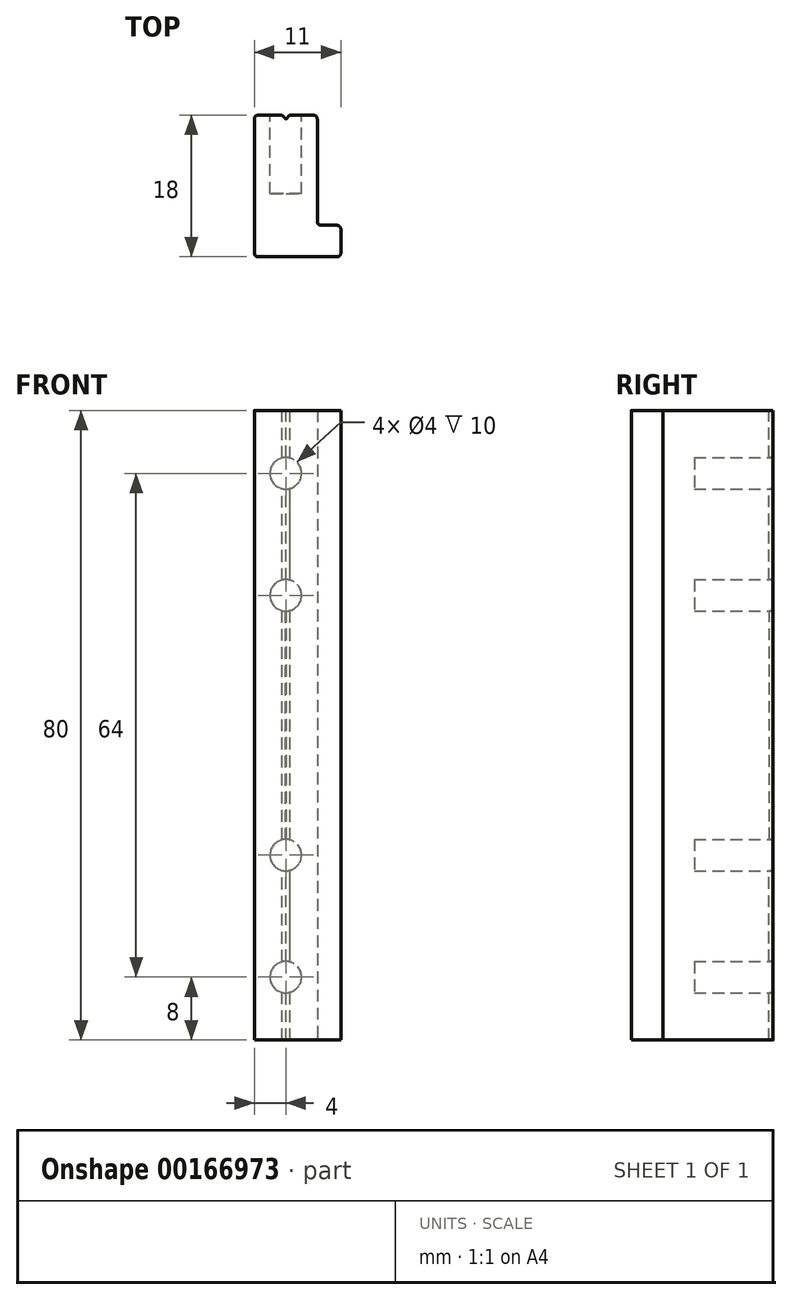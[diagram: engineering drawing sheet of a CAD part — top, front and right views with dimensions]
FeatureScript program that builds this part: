
annotation { "Feature Type Name" : "Feature", "Feature Type Description" : "" }
export const myFeature = defineFeature(function(context is Context, id is Id, definition is map)
    precondition{}
    {
        {
            var Q0;
            Q0=qCreatedBy(makeId("Top.planeOp"),FACE);
            var sketch = newSketch(context, id + "F0", { "sketchPlane" : qUnion([Q0])});
            skLineSegment(sketch, "E0", {"start": v(0, 0) * mm, "end": v(0, 18) * mm});
            skLineSegment(sketch, "E1", {"start": v(0, 18) * mm, "end": v(8, 18) * mm});
            skLineSegment(sketch, "E2", {"start": v(8, 18) * mm, "end": v(8, 4) * mm});
            skLineSegment(sketch, "E3", {"start": v(8, 4) * mm, "end": v(11, 4) * mm});
            skLineSegment(sketch, "E4", {"start": v(11, 4) * mm, "end": v(11, 0) * mm});
            skLineSegment(sketch, "E5", {"start": v(11, 0) * mm, "end": v(0, 0) * mm});
            skSolve(sketch);
        }
        {
            var Q0;
            Q0=makeQuery(id+"F0.imprint","IMPRINT",FACE,{"disambiguationData":[TD([[makeQuery(id+"F0.imprint","IMPRINT",EDGE,{"derivedFrom":sQuery(id+"F0.wireOp",EDGE,"E0")}),-1.0]])]});
            extrude(context, id + "F1", {"entities" : qUnion([Q0]), "depth" : 80 * mm});
        }
        {
            var Q0;
            Q0=makeQuery(id+"F1.opExtrude","SWEPT_FACE",FACE,{"disambiguationData":[OSD([sQuery(id+"F0.wireOp",EDGE,"E1")])]});
            var sketch = newSketch(context, id + "F2", { "sketchPlane" : qUnion([Q0])});
            skCircle(sketch, "E6", {"center": v(-4, 72) * mm, "radius": 2 * mm});
            skCircle(sketch, "E7", {"center": v(-4, 56.5) * mm, "radius": 2 * mm});
            skCircle(sketch, "E8", {"center": v(-4, 23.5) * mm, "radius": 2 * mm});
            skCircle(sketch, "E9", {"center": v(-4, 8) * mm, "radius": 2 * mm});
            skLineSegment(sketch, "E10", {"start": v(-4, 80) * mm, "end": v(-4, 0) * mm, "construction": true});
            skSolve(sketch);
        }
        {
            var Q0;
            Q0=makeQuery(id+"F2.imprint","IMPRINT",FACE,{"disambiguationData":[TD([[makeQuery(id+"F2.imprint","IMPRINT",EDGE,{"derivedFrom":sQuery(id+"F2.wireOp",EDGE,"E6")}),1.0]])]});
            var Q1;
            Q1=makeQuery(id+"F2.imprint","IMPRINT",FACE,{"disambiguationData":[TD([[makeQuery(id+"F2.imprint","IMPRINT",EDGE,{"derivedFrom":sQuery(id+"F2.wireOp",EDGE,"E7")}),1.0]])]});
            var Q2;
            Q2=makeQuery(id+"F2.imprint","IMPRINT",FACE,{"disambiguationData":[TD([[makeQuery(id+"F2.imprint","IMPRINT",EDGE,{"derivedFrom":sQuery(id+"F2.wireOp",EDGE,"E8")}),1.0]])]});
            var Q3;
            Q3=makeQuery(id+"F2.imprint","IMPRINT",FACE,{"disambiguationData":[TD([[makeQuery(id+"F2.imprint","IMPRINT",EDGE,{"derivedFrom":sQuery(id+"F2.wireOp",EDGE,"E9")}),1.0]])]});
            extrude(context, id + "F3", {"entities" : qUnion([Q0, Q1, Q2, Q3]), "operationType" : NewBodyOperationType.REMOVE, "oppositeDirection" : true, "depth" : 10 * mm});
        }
        {
            var Q0;
            Q0=makeQuery(id+"F1.opExtrude","CAP_FACE",FACE,{"disambiguationData":[OSD([sQuery(id+"F0.wireOp",EDGE,"E0"),sQuery(id+"F0.wireOp",EDGE,"E1"),sQuery(id+"F0.wireOp",EDGE,"E2"),sQuery(id+"F0.wireOp",EDGE,"E3"),sQuery(id+"F0.wireOp",EDGE,"E4"),sQuery(id+"F0.wireOp",EDGE,"E5")])],"isStart":false});
            var sketch = newSketch(context, id + "F4", { "sketchPlane" : qUnion([Q0])});
            skLineSegment(sketch, "E11", {"start": v(4, 18) * mm, "end": v(4, 0) * mm, "construction": true});
            skLineSegment(sketch, "E12", {"start": v(3.5, 18) * mm, "end": v(4.5, 18) * mm});
            skLineSegment(sketch, "E13", {"start": v(3.5, 18) * mm, "end": v(4, 17.47) * mm});
            skLineSegment(sketch, "E14", {"start": v(4, 17.47) * mm, "end": v(4.5, 18) * mm});
            skSolve(sketch);
        }
        {
            var Q0;
            Q0=makeQuery(id+"F4.imprint","IMPRINT",FACE,{"disambiguationData":[TD([[makeQuery(id+"F4.imprint","IMPRINT",EDGE,{"derivedFrom":sQuery(id+"F4.wireOp",EDGE,"E12")}),-1.0]])]});
            extrude(context, id + "F5", {"entities" : qUnion([Q0]), "operationType" : NewBodyOperationType.REMOVE, "oppositeDirection" : true, "depth" : 100 * mm});
        }
        {
            var Q0;
            {var subQ0=sQuery(id+"F0.wireOp",EDGE,"E1");var subQ1=sQuery(id+"F4.wireOp",EDGE,"E14");Q0=makeQuery(id+"F5.boolean.opBoolean","COPY",EDGE,{"disambiguationData":[TD([makeQuery(id+"F1.opExtrude","CAP_FACE",FACE,{"disambiguationData":[OSD([sQuery(id+"F0.wireOp",EDGE,"E0"),subQ0,sQuery(id+"F0.wireOp",EDGE,"E2"),sQuery(id+"F0.wireOp",EDGE,"E3"),sQuery(id+"F0.wireOp",EDGE,"E4"),sQuery(id+"F0.wireOp",EDGE,"E5")])],"isStart":false}),makeQuery(id+"F1.opExtrude","SWEPT_FACE",FACE,{"disambiguationData":[OSD([subQ0])]}),makeQuery(id+"F3.boolean.opBoolean","COPY",FACE,{"derivedFrom":makeQuery(id+"F3.opExtrude","SWEPT_FACE",FACE,{"disambiguationData":[OSD([sQuery(id+"F2.wireOp",EDGE,"E6")])]})}),makeQuery(id+"F5.opExtrude","SWEPT_FACE",FACE,{"disambiguationData":[OSD([subQ1])]})])],"derivedFrom":makeQuery(id+"F5.opExtrude","SWEPT_EDGE",EDGE,{"disambiguationData":[OSD([subQ0,sQuery(id+"F4.wireOp",EDGE,"E12"),subQ1])]})});}
            var Q1;
            {var subQ0=sQuery(id+"F0.wireOp",EDGE,"E1");var subQ1=sQuery(id+"F4.wireOp",EDGE,"E13");Q1=makeQuery(id+"F5.boolean.opBoolean","COPY",EDGE,{"disambiguationData":[TD([makeQuery(id+"F1.opExtrude","CAP_FACE",FACE,{"disambiguationData":[OSD([sQuery(id+"F0.wireOp",EDGE,"E0"),subQ0,sQuery(id+"F0.wireOp",EDGE,"E2"),sQuery(id+"F0.wireOp",EDGE,"E3"),sQuery(id+"F0.wireOp",EDGE,"E4"),sQuery(id+"F0.wireOp",EDGE,"E5")])],"isStart":false}),makeQuery(id+"F1.opExtrude","SWEPT_FACE",FACE,{"disambiguationData":[OSD([subQ0])]}),makeQuery(id+"F3.boolean.opBoolean","COPY",FACE,{"derivedFrom":makeQuery(id+"F3.opExtrude","SWEPT_FACE",FACE,{"disambiguationData":[OSD([sQuery(id+"F2.wireOp",EDGE,"E6")])]})}),makeQuery(id+"F5.opExtrude","SWEPT_FACE",FACE,{"disambiguationData":[OSD([subQ1])]})])],"derivedFrom":makeQuery(id+"F5.opExtrude","SWEPT_EDGE",EDGE,{"disambiguationData":[OSD([subQ0,sQuery(id+"F4.wireOp",EDGE,"E12"),subQ1])]})});}
            var Q2;
            {var subQ0=sQuery(id+"F0.wireOp",EDGE,"E1");var subQ1=sQuery(id+"F4.wireOp",EDGE,"E13");Q2=makeQuery(id+"F5.boolean.opBoolean","COPY",EDGE,{"disambiguationData":[TD([makeQuery(id+"F1.opExtrude","SWEPT_FACE",FACE,{"disambiguationData":[OSD([subQ0])]}),makeQuery(id+"F3.boolean.opBoolean","COPY",FACE,{"derivedFrom":makeQuery(id+"F3.opExtrude","SWEPT_FACE",FACE,{"disambiguationData":[OSD([sQuery(id+"F2.wireOp",EDGE,"E6")])]})}),makeQuery(id+"F3.boolean.opBoolean","COPY",FACE,{"derivedFrom":makeQuery(id+"F3.opExtrude","SWEPT_FACE",FACE,{"disambiguationData":[OSD([sQuery(id+"F2.wireOp",EDGE,"E7")])]})}),makeQuery(id+"F5.opExtrude","SWEPT_FACE",FACE,{"disambiguationData":[OSD([subQ1])]})])],"derivedFrom":makeQuery(id+"F5.opExtrude","SWEPT_EDGE",EDGE,{"disambiguationData":[OSD([subQ0,sQuery(id+"F4.wireOp",EDGE,"E12"),subQ1])]})});}
            var Q3;
            {var subQ0=sQuery(id+"F0.wireOp",EDGE,"E1");var subQ1=sQuery(id+"F4.wireOp",EDGE,"E14");Q3=makeQuery(id+"F5.boolean.opBoolean","COPY",EDGE,{"disambiguationData":[TD([makeQuery(id+"F1.opExtrude","SWEPT_FACE",FACE,{"disambiguationData":[OSD([subQ0])]}),makeQuery(id+"F3.boolean.opBoolean","COPY",FACE,{"derivedFrom":makeQuery(id+"F3.opExtrude","SWEPT_FACE",FACE,{"disambiguationData":[OSD([sQuery(id+"F2.wireOp",EDGE,"E6")])]})}),makeQuery(id+"F3.boolean.opBoolean","COPY",FACE,{"derivedFrom":makeQuery(id+"F3.opExtrude","SWEPT_FACE",FACE,{"disambiguationData":[OSD([sQuery(id+"F2.wireOp",EDGE,"E7")])]})}),makeQuery(id+"F5.opExtrude","SWEPT_FACE",FACE,{"disambiguationData":[OSD([subQ1])]})])],"derivedFrom":makeQuery(id+"F5.opExtrude","SWEPT_EDGE",EDGE,{"disambiguationData":[OSD([subQ0,sQuery(id+"F4.wireOp",EDGE,"E12"),subQ1])]})});}
            var Q4;
            {var subQ0=sQuery(id+"F4.wireOp",EDGE,"E14");var subQ1=sQuery(id+"F4.wireOp",EDGE,"E13");Q4=makeQuery(id+"F5.boolean.opBoolean","COPY",EDGE,{"disambiguationData":[TD([makeQuery(id+"F3.boolean.opBoolean","COPY",FACE,{"derivedFrom":makeQuery(id+"F3.opExtrude","SWEPT_FACE",FACE,{"disambiguationData":[OSD([sQuery(id+"F2.wireOp",EDGE,"E7")])]})}),makeQuery(id+"F3.boolean.opBoolean","COPY",FACE,{"derivedFrom":makeQuery(id+"F3.opExtrude","SWEPT_FACE",FACE,{"disambiguationData":[OSD([sQuery(id+"F2.wireOp",EDGE,"E8")])]})}),makeQuery(id+"F5.opExtrude","SWEPT_FACE",FACE,{"disambiguationData":[OSD([subQ1])]}),makeQuery(id+"F5.opExtrude","SWEPT_FACE",FACE,{"disambiguationData":[OSD([subQ0])]})])],"derivedFrom":makeQuery(id+"F5.opExtrude","SWEPT_EDGE",EDGE,{"disambiguationData":[OSD([subQ1,subQ0])]})});}
            var Q5;
            {var subQ0=sQuery(id+"F0.wireOp",EDGE,"E1");var subQ1=sQuery(id+"F4.wireOp",EDGE,"E14");Q5=makeQuery(id+"F5.boolean.opBoolean","COPY",EDGE,{"disambiguationData":[TD([makeQuery(id+"F1.opExtrude","SWEPT_FACE",FACE,{"disambiguationData":[OSD([subQ0])]}),makeQuery(id+"F3.boolean.opBoolean","COPY",FACE,{"derivedFrom":makeQuery(id+"F3.opExtrude","SWEPT_FACE",FACE,{"disambiguationData":[OSD([sQuery(id+"F2.wireOp",EDGE,"E7")])]})}),makeQuery(id+"F3.boolean.opBoolean","COPY",FACE,{"derivedFrom":makeQuery(id+"F3.opExtrude","SWEPT_FACE",FACE,{"disambiguationData":[OSD([sQuery(id+"F2.wireOp",EDGE,"E8")])]})}),makeQuery(id+"F5.opExtrude","SWEPT_FACE",FACE,{"disambiguationData":[OSD([subQ1])]})])],"derivedFrom":makeQuery(id+"F5.opExtrude","SWEPT_EDGE",EDGE,{"disambiguationData":[OSD([subQ0,sQuery(id+"F4.wireOp",EDGE,"E12"),subQ1])]})});}
            var Q6;
            {var subQ0=sQuery(id+"F0.wireOp",EDGE,"E1");var subQ1=sQuery(id+"F4.wireOp",EDGE,"E14");Q6=makeQuery(id+"F5.boolean.opBoolean","COPY",EDGE,{"disambiguationData":[TD([makeQuery(id+"F1.opExtrude","SWEPT_FACE",FACE,{"disambiguationData":[OSD([subQ0])]}),makeQuery(id+"F3.boolean.opBoolean","COPY",FACE,{"derivedFrom":makeQuery(id+"F3.opExtrude","SWEPT_FACE",FACE,{"disambiguationData":[OSD([sQuery(id+"F2.wireOp",EDGE,"E8")])]})}),makeQuery(id+"F3.boolean.opBoolean","COPY",FACE,{"derivedFrom":makeQuery(id+"F3.opExtrude","SWEPT_FACE",FACE,{"disambiguationData":[OSD([sQuery(id+"F2.wireOp",EDGE,"E9")])]})}),makeQuery(id+"F5.opExtrude","SWEPT_FACE",FACE,{"disambiguationData":[OSD([subQ1])]})])],"derivedFrom":makeQuery(id+"F5.opExtrude","SWEPT_EDGE",EDGE,{"disambiguationData":[OSD([subQ0,sQuery(id+"F4.wireOp",EDGE,"E12"),subQ1])]})});}
            var Q7;
            {var subQ0=sQuery(id+"F0.wireOp",EDGE,"E1");var subQ1=sQuery(id+"F4.wireOp",EDGE,"E13");Q7=makeQuery(id+"F5.boolean.opBoolean","COPY",EDGE,{"disambiguationData":[TD([makeQuery(id+"F1.opExtrude","SWEPT_FACE",FACE,{"disambiguationData":[OSD([subQ0])]}),makeQuery(id+"F3.boolean.opBoolean","COPY",FACE,{"derivedFrom":makeQuery(id+"F3.opExtrude","SWEPT_FACE",FACE,{"disambiguationData":[OSD([sQuery(id+"F2.wireOp",EDGE,"E8")])]})}),makeQuery(id+"F3.boolean.opBoolean","COPY",FACE,{"derivedFrom":makeQuery(id+"F3.opExtrude","SWEPT_FACE",FACE,{"disambiguationData":[OSD([sQuery(id+"F2.wireOp",EDGE,"E9")])]})}),makeQuery(id+"F5.opExtrude","SWEPT_FACE",FACE,{"disambiguationData":[OSD([subQ1])]})])],"derivedFrom":makeQuery(id+"F5.opExtrude","SWEPT_EDGE",EDGE,{"disambiguationData":[OSD([subQ0,sQuery(id+"F4.wireOp",EDGE,"E12"),subQ1])]})});}
            var Q8;
            {var subQ0=sQuery(id+"F0.wireOp",EDGE,"E1");var subQ1=sQuery(id+"F4.wireOp",EDGE,"E13");Q8=makeQuery(id+"F5.boolean.opBoolean","COPY",EDGE,{"disambiguationData":[TD([makeQuery(id+"F1.opExtrude","CAP_FACE",FACE,{"disambiguationData":[OSD([sQuery(id+"F0.wireOp",EDGE,"E0"),subQ0,sQuery(id+"F0.wireOp",EDGE,"E2"),sQuery(id+"F0.wireOp",EDGE,"E3"),sQuery(id+"F0.wireOp",EDGE,"E4"),sQuery(id+"F0.wireOp",EDGE,"E5")])],"isStart":true}),makeQuery(id+"F1.opExtrude","SWEPT_FACE",FACE,{"disambiguationData":[OSD([subQ0])]}),makeQuery(id+"F3.boolean.opBoolean","COPY",FACE,{"derivedFrom":makeQuery(id+"F3.opExtrude","SWEPT_FACE",FACE,{"disambiguationData":[OSD([sQuery(id+"F2.wireOp",EDGE,"E9")])]})}),makeQuery(id+"F5.opExtrude","SWEPT_FACE",FACE,{"disambiguationData":[OSD([subQ1])]})])],"derivedFrom":makeQuery(id+"F5.opExtrude","SWEPT_EDGE",EDGE,{"disambiguationData":[OSD([subQ0,sQuery(id+"F4.wireOp",EDGE,"E12"),subQ1])]})});}
            var Q9;
            {var subQ0=sQuery(id+"F0.wireOp",EDGE,"E1");var subQ1=sQuery(id+"F4.wireOp",EDGE,"E14");Q9=makeQuery(id+"F5.boolean.opBoolean","COPY",EDGE,{"disambiguationData":[TD([makeQuery(id+"F1.opExtrude","CAP_FACE",FACE,{"disambiguationData":[OSD([sQuery(id+"F0.wireOp",EDGE,"E0"),subQ0,sQuery(id+"F0.wireOp",EDGE,"E2"),sQuery(id+"F0.wireOp",EDGE,"E3"),sQuery(id+"F0.wireOp",EDGE,"E4"),sQuery(id+"F0.wireOp",EDGE,"E5")])],"isStart":true}),makeQuery(id+"F1.opExtrude","SWEPT_FACE",FACE,{"disambiguationData":[OSD([subQ0])]}),makeQuery(id+"F3.boolean.opBoolean","COPY",FACE,{"derivedFrom":makeQuery(id+"F3.opExtrude","SWEPT_FACE",FACE,{"disambiguationData":[OSD([sQuery(id+"F2.wireOp",EDGE,"E9")])]})}),makeQuery(id+"F5.opExtrude","SWEPT_FACE",FACE,{"disambiguationData":[OSD([subQ1])]})])],"derivedFrom":makeQuery(id+"F5.opExtrude","SWEPT_EDGE",EDGE,{"disambiguationData":[OSD([subQ0,sQuery(id+"F4.wireOp",EDGE,"E12"),subQ1])]})});}
            chamfer(context, id + "F6", {"entities" : qUnion([Q0, Q1, Q2, Q3, Q4, Q5, Q6, Q7, Q8, Q9]), "width" : 0.1 * mm, "tangentPropagation" : true});
        }
        {
            var Q0;
            Q0=makeQuery(id+"F1.opExtrude","SWEPT_EDGE",EDGE,{"disambiguationData":[OSD([sQuery(id+"F0.wireOp",EDGE,"E0"),sQuery(id+"F0.wireOp",EDGE,"E5")])]});
            var Q1;
            Q1=makeQuery(id+"F1.opExtrude","SWEPT_EDGE",EDGE,{"disambiguationData":[OSD([sQuery(id+"F0.wireOp",EDGE,"E4"),sQuery(id+"F0.wireOp",EDGE,"E5")])]});
            var Q2;
            Q2=makeQuery(id+"F1.opExtrude","SWEPT_EDGE",EDGE,{"disambiguationData":[OSD([sQuery(id+"F0.wireOp",EDGE,"E3"),sQuery(id+"F0.wireOp",EDGE,"E4")])]});
            var Q3;
            Q3=makeQuery(id+"F1.opExtrude","SWEPT_EDGE",EDGE,{"disambiguationData":[OSD([sQuery(id+"F0.wireOp",EDGE,"E1"),sQuery(id+"F0.wireOp",EDGE,"E2")])]});
            var Q4;
            Q4=makeQuery(id+"F1.opExtrude","SWEPT_EDGE",EDGE,{"disambiguationData":[OSD([sQuery(id+"F0.wireOp",EDGE,"E0"),sQuery(id+"F0.wireOp",EDGE,"E1")])]});
            fillet(context, id + "F7", {"entities" : qUnion([Q0, Q1, Q2, Q3, Q4]), "radius" : 0.5 * mm, "tangentPropagation" : true, "allowEdgeOverflow" : false});
        }
        {
            var Q0;
            Q0=makeQuery(id+"F1.opExtrude","SWEPT_EDGE",EDGE,{"disambiguationData":[OSD([sQuery(id+"F0.wireOp",EDGE,"E2"),sQuery(id+"F0.wireOp",EDGE,"E3")])]});
            fillet(context, id + "F8", {"entities" : qUnion([Q0]), "radius" : 0.5 * mm, "tangentPropagation" : true, "allowEdgeOverflow" : false});
        }
    });
